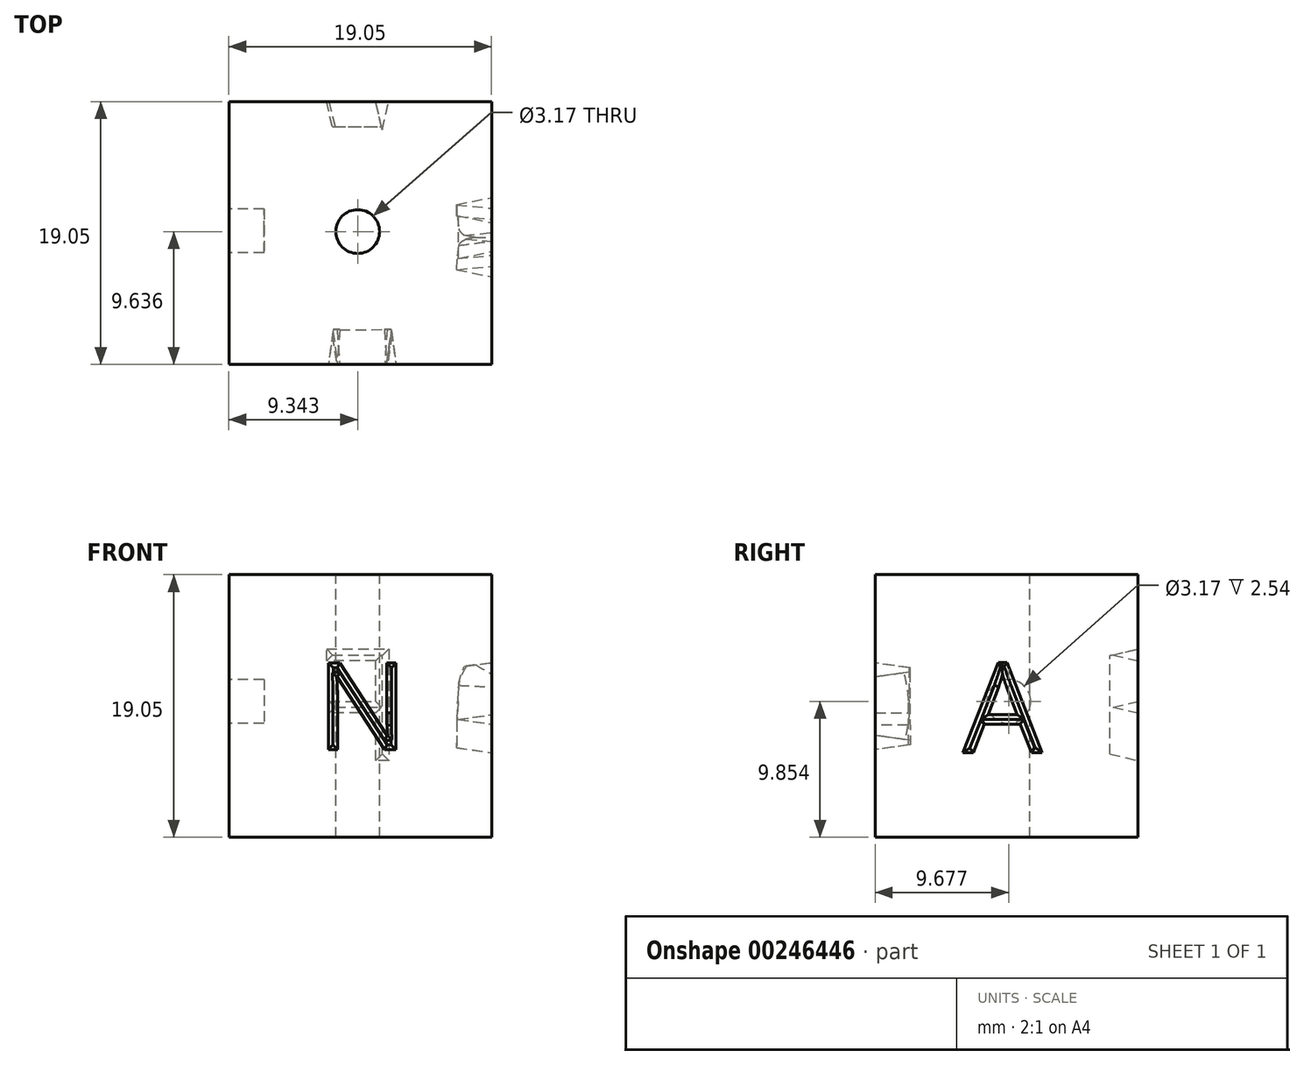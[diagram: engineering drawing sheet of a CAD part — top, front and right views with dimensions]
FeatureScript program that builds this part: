
annotation { "Feature Type Name" : "Feature", "Feature Type Description" : "" }
export const myFeature = defineFeature(function(context is Context, id is Id, definition is map)
    precondition{}
    {
        {
            var Q0;
            Q0=qCreatedBy(makeId("Top.planeOp"),FACE);
            var sketch = newSketch(context, id + "F0", { "sketchPlane" : qUnion([Q0])});
            skLineSegment(sketch, "E0.bottom", {"start": v(0.17, 31.62) * mm, "end": v(19.22, 31.62) * mm});
            skLineSegment(sketch, "E0.top", {"start": v(0.17, 12.57) * mm, "end": v(19.22, 12.57) * mm});
            skLineSegment(sketch, "E0.left", {"start": v(0.17, 31.62) * mm, "end": v(0.17, 12.57) * mm});
            skLineSegment(sketch, "E0.right", {"start": v(19.22, 31.62) * mm, "end": v(19.22, 12.57) * mm});
            skSolve(sketch);
        }
        {
            var Q0;
            Q0 = qSketchRegion(id + "F0", true);
            extrude(context, id + "F1", {"entities" : qUnion([Q0]), "depth" : 19.05 * mm});
        }
        {
            var Q0;
            Q0=makeQuery(id+"F1.opExtrude","CAP_FACE",FACE,{"disambiguationData":[OSD([sQuery(id+"F0.wireOp",EDGE,"E0.bottom"),sQuery(id+"F0.wireOp",EDGE,"E0.top"),sQuery(id+"F0.wireOp",EDGE,"E0.left"),sQuery(id+"F0.wireOp",EDGE,"E0.right")])],"isStart":false});
            var sketch = newSketch(context, id + "F2", { "sketchPlane" : qUnion([Q0])});
            skCircle(sketch, "E1", {"center": v(9.51, 22.2) * mm, "radius": 1.59 * mm});
            skSolve(sketch);
        }
        {
            var Q0;
            Q0=makeQuery(id+"F2.imprint","IMPRINT",FACE,{"disambiguationData":[TD([[makeQuery(id+"F2.imprint","IMPRINT",EDGE,{"derivedFrom":sQuery(id+"F2.wireOp",EDGE,"E1")}),1.0]])]});
            extrude(context, id + "F3", {"entities" : qUnion([Q0]), "operationType" : NewBodyOperationType.REMOVE, "endBound" : BoundingType.THROUGH_ALL, "oppositeDirection" : true, "depth" : 25.4 * mm});
        }
        {
            var Q0;
            Q0=makeQuery(id+"F1.opExtrude","SWEPT_FACE",FACE,{"disambiguationData":[OSD([sQuery(id+"F0.wireOp",EDGE,"E0.top")])]});
            var sketch = newSketch(context, id + "F4", { "sketchPlane" : qUnion([Q0])});
            skText(sketch, "E2", { "text": "N", "fontName": "OpenSans-Regular.ttf"});
            const initialGuessF4  = {"E2": [0.00652, 0.00636, 1, 0, 0.00634]};
            skSetInitialGuess(sketch, initialGuessF4);
            skSolve(sketch);
        }
        {
            var Q0;
            Q0=makeQuery(id+"F4.imprint","IMPRINT",FACE,{"disambiguationData":[TD([[makeQuery(id+"F4.imprint","IMPRINT",EDGE,{"derivedFrom":sQuery(id+"F4.wireOp",EDGE,"E2.sketch_text.stroke-0")}),-1.0]])]});
            extrude(context, id + "F5", {"entities" : qUnion([Q0]), "operationType" : NewBodyOperationType.REMOVE, "oppositeDirection" : true, "depth" : 2.54 * mm, "hasDraft" : true, "draftAngle" : 8 * degree, "draftPullDirection" : true});
        }
        {
            var Q0;
            Q0=makeQuery(id+"F1.opExtrude","SWEPT_FACE",FACE,{"disambiguationData":[OSD([sQuery(id+"F0.wireOp",EDGE,"E0.right")])]});
            var sketch = newSketch(context, id + "F6", { "sketchPlane" : qUnion([Q0])});
            skText(sketch, "E3", { "text": "A", "fontName": "OpenSans-Regular.ttf"});
            const initialGuessF6  = {"E3": [0.01892, 0.00615, 1, 0, 0.00655]};
            skSetInitialGuess(sketch, initialGuessF6);
            skSolve(sketch);
        }
        {
            var Q0;
            Q0 = qSketchRegion(id + "F6", true);
            extrude(context, id + "F7", {"entities" : qUnion([Q0]), "operationType" : NewBodyOperationType.REMOVE, "oppositeDirection" : true, "depth" : 2.54 * mm, "hasDraft" : true, "draftAngle" : 8 * degree, "draftPullDirection" : true});
        }
        {
            var Q0;
            Q0=makeQuery(id+"F1.opExtrude","SWEPT_FACE",FACE,{"disambiguationData":[OSD([sQuery(id+"F0.wireOp",EDGE,"E0.bottom")])]});
            var sketch = newSketch(context, id + "F8", { "sketchPlane" : qUnion([Q0])});
            skText(sketch, "E4", { "text": "F", "fontName": "OpenSans-Regular.ttf"});
            const initialGuessF8  = {"E4": [-0.01287, 0.00557, 1, 0, 0.00815]};
            skSetInitialGuess(sketch, initialGuessF8);
            skSolve(sketch);
        }
        {
            var Q0;
            Q0 = qSketchRegion(id + "F8", true);
            extrude(context, id + "F9", {"entities" : qUnion([Q0]), "operationType" : NewBodyOperationType.REMOVE, "oppositeDirection" : true, "depth" : 2.54 * mm, "hasDraft" : true, "draftAngle" : 13 * degree, "draftPullDirection" : true});
        }
        {
            var Q0;
            Q0=makeQuery(id+"F1.opExtrude","SWEPT_FACE",FACE,{"disambiguationData":[OSD([sQuery(id+"F0.wireOp",EDGE,"E0.left")])]});
            var sketch = newSketch(context, id + "F10", { "sketchPlane" : qUnion([Q0])});
            skCircle(sketch, "E5", {"center": v(-22.25, 9.85) * mm, "radius": 1.59 * mm});
            skSolve(sketch);
        }
        {
            var Q0;
            Q0 = qSketchRegion(id + "F10", true);
            extrude(context, id + "F11", {"entities" : qUnion([Q0]), "operationType" : NewBodyOperationType.REMOVE, "oppositeDirection" : true, "depth" : 2.54 * mm});
        }
    });
